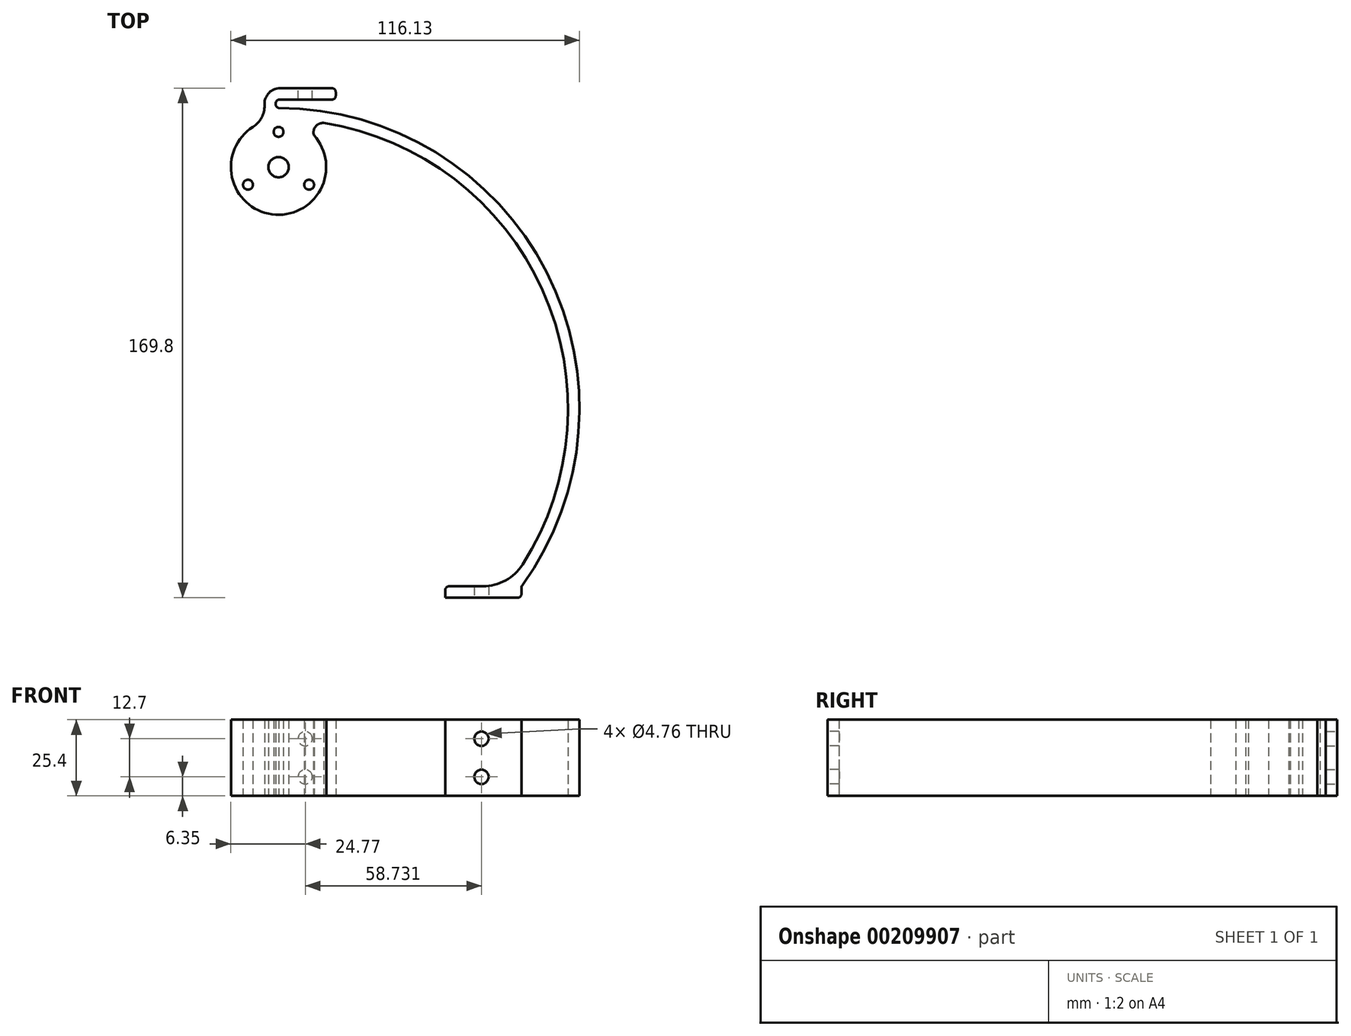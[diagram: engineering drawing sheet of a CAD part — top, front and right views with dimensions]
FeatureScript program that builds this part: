
annotation { "Feature Type Name" : "Feature", "Feature Type Description" : "" }
export const myFeature = defineFeature(function(context is Context, id is Id, definition is map)
    precondition{}
    {
        {
            var Q0;
            Q0=qCreatedBy(makeId("Top.planeOp"),FACE);
            var sketch = newSketch(context, id + "F0", { "sketchPlane" : qUnion([Q0])});
            skCircle(sketch, "E0", {"center": v(0, 0) * mm, "radius": 15.88 * mm});
            skCircle(sketch, "E1", {"center": v(0, 0) * mm, "radius": 3.38 * mm});
            skArc(sketch, "E2", {"start": v(76.2, -139.7) * mm, "mid": v(0, 15.88) * mm, "end": v(-76.2, -139.7) * mm});
            skLineSegment(sketch, "E3", {"start": v(-76.2, -139.7) * mm, "end": v(76.2, -139.7) * mm, "construction": true});
            skLineSegment(sketch, "E4", {"start": v(0, 15.88) * mm, "end": v(0, -139.7) * mm, "construction": true});
            skArc(sketch, "E5.0", {"start": v(81.2, -139.37) * mm, "mid": v(-0.2, 19.67) * mm, "end": v(-80.96, -139.7) * mm});
            skLineSegment(sketch, "E6", {"start": v(56.83, -139.7) * mm, "end": v(80.96, -139.7) * mm, "construction": true});
            skLineSegment(sketch, "E7", {"start": v(76.2, -139.7) * mm, "end": v(55.56, -139.7) * mm});
            skLineSegment(sketch, "E8", {"start": v(55.56, -140.97) * mm, "end": v(55.56, -143.5) * mm});
            skLineSegment(sketch, "E9", {"start": v(55.56, -143.5) * mm, "end": v(79.69, -143.5) * mm});
            skLineSegment(sketch, "E10", {"start": v(80.96, -142.23) * mm, "end": v(80.96, -140.11) * mm});
            skLineSegment(sketch, "E11", {"start": v(0, 19.67) * mm, "end": v(0, 15.88) * mm});
            skLineSegment(sketch, "E12.bottom", {"start": v(0, 26.3) * mm, "end": v(17.78, 26.3) * mm});
            skLineSegment(sketch, "E12.top", {"start": v(0, 22.5) * mm, "end": v(17.78, 22.5) * mm});
            skLineSegment(sketch, "E12.left", {"start": v(0, 26.3) * mm, "end": v(0, 22.5) * mm});
            skLineSegment(sketch, "E12.right", {"start": v(19.05, 25.03) * mm, "end": v(19.05, 23.77) * mm});
            skArc(sketch, "E13", {"start": v(0, 22.5) * mm, "mid": v(-1, 21.09) * mm, "end": v(0, 19.68) * mm});
            skArc(sketch, "E14", {"start": v(0, 26.3) * mm, "mid": v(-4.68, 21.09) * mm, "end": v(0, 15.88) * mm});
            skPoint(sketch, "E15.visualSharp", {"position": v(19.05, 26.3) * mm});
            skArc(sketch, "E15.filletArc", {"start": v(19.05, 25.03) * mm, "mid": v(18.68, 25.93) * mm, "end": v(17.78, 26.3) * mm});
            skPoint(sketch, "E16.visualSharp", {"position": v(19.05, 22.5) * mm});
            skArc(sketch, "E16.filletArc", {"start": v(17.78, 22.5) * mm, "mid": v(18.68, 22.87) * mm, "end": v(19.05, 23.77) * mm});
            skPoint(sketch, "E17.visualSharp", {"position": v(80.96, -143.5) * mm});
            skArc(sketch, "E17.filletArc", {"start": v(79.69, -143.5) * mm, "mid": v(80.58, -143.13) * mm, "end": v(80.96, -142.23) * mm});
            skPoint(sketch, "E18.visualSharp", {"position": v(80.96, -139.7) * mm});
            skArc(sketch, "E18.filletArc", {"start": v(81.2, -139.37) * mm, "mid": v(81.02, -139.72) * mm, "end": v(80.96, -140.11) * mm});
            skPoint(sketch, "E19.newPointB", {"position": v(55.56, -139.7) * mm});
            skArc(sketch, "E19.filletArc", {"start": v(56.83, -139.7) * mm, "mid": v(55.93, -140.07) * mm, "end": v(55.56, -140.97) * mm});
            skLineSegment(sketch, "E20", {"start": v(55.56, -139.7) * mm, "end": v(55.56, -140.97) * mm, "construction": true});
            skLineSegment(sketch, "E21", {"start": v(79.69, -143.5) * mm, "end": v(80.96, -143.5) * mm, "construction": true});
            skLineSegment(sketch, "E22", {"start": v(80.96, -142.23) * mm, "end": v(80.96, -143.5) * mm, "construction": true});
            skArc(sketch, "E23", {"start": v(-8.52, 13.4) * mm, "mid": v(-5.53, 16.7) * mm, "end": v(-4.68, 21.09) * mm});
            skArc(sketch, "E24", {"start": v(15.43, 14.63) * mm, "mid": v(11.9, 12.78) * mm, "end": v(13.1, 8.97) * mm});
            skCircle(sketch, "E25", {"center": v(0, 0) * mm, "radius": 11.75 * mm, "construction": true});
            skCircle(sketch, "E26", {"center": v(0, 11.75) * mm, "radius": 1.65 * mm});
            skCircle(sketch, "E27", {"center": v(10.17, -5.87) * mm, "radius": 1.65 * mm});
            skCircle(sketch, "E28", {"center": v(-10.17, -5.87) * mm, "radius": 1.65 * mm});
            skLineSegment(sketch, "E29", {"start": v(0, 11.75) * mm, "end": v(-10.17, -5.87) * mm, "construction": true});
            skLineSegment(sketch, "E30", {"start": v(10.17, -5.87) * mm, "end": v(0, 11.75) * mm, "construction": true});
            skLineSegment(sketch, "E31", {"start": v(10.17, -5.87) * mm, "end": v(-10.17, -5.87) * mm, "construction": true});
            skLineSegment(sketch, "E32", {"start": v(-10.17, -5.87) * mm, "end": v(5.09, 2.94) * mm, "construction": true});
            skSolve(sketch);
        }
        {
            var Q0;
            Q0 = qSketchRegion(id + "F0", true);
            extrude(context, id + "F1", {"entities" : qUnion([Q0]), "depth" : 25.4 * mm});
        }
        {
            var Q0;
            Q0=makeQuery(id+"F1.opExtrude","SWEPT_EDGE",EDGE,{"disambiguationData":[OSD([sQuery(id+"F0.wireOp",EDGE,"E2"),sQuery(id+"F0.wireOp",EDGE,"E7")])]});
            fillet(context, id + "F2", {"entities" : qUnion([Q0]), "radius" : 15.66 * mm, "tangentPropagation" : true, "allowEdgeOverflow" : false});
        }
        {
            var Q0;
            Q0=makeQuery(id+"F1.opExtrude","SWEPT_FACE",FACE,{"disambiguationData":[OSD([sQuery(id+"F0.wireOp",EDGE,"E9")])]});
            var sketch = newSketch(context, id + "F3", { "sketchPlane" : qUnion([Q0])});
            skLineSegment(sketch, "E33", {"start": v(67.62, 25.4) * mm, "end": v(67.62, 0) * mm, "construction": true});
            skPoint(sketch, "E34", {"position": v(67.62, 19.05) * mm});
            skPoint(sketch, "E35", {"position": v(67.62, 6.35) * mm});
            skSolve(sketch);
        }
        {
            var Q0;
            Q0=sQuery(id+"F3.wireOp",VERTEX,"E34");
            var Q1;
            Q1=sQuery(id+"F3.wireOp",VERTEX,"E35");
            var Q2;
            Q2=makeQuery(id+"F1.opExtrude","SWEPT_BODY",BODY,{"disambiguationData":[OSD([sQuery(id+"F0.wireOp",EDGE,"E0"),sQuery(id+"F0.wireOp",EDGE,"E1"),sQuery(id+"F0.wireOp",EDGE,"E2"),sQuery(id+"F0.wireOp",EDGE,"E5.0"),sQuery(id+"F0.wireOp",EDGE,"E7"),sQuery(id+"F0.wireOp",EDGE,"E8"),sQuery(id+"F0.wireOp",EDGE,"E9"),sQuery(id+"F0.wireOp",EDGE,"E10"),sQuery(id+"F0.wireOp",EDGE,"E12.bottom"),sQuery(id+"F0.wireOp",EDGE,"E12.top"),sQuery(id+"F0.wireOp",EDGE,"E12.right"),sQuery(id+"F0.wireOp",EDGE,"E13"),sQuery(id+"F0.wireOp",EDGE,"E14"),sQuery(id+"F0.wireOp",EDGE,"E15.filletArc"),sQuery(id+"F0.wireOp",EDGE,"E16.filletArc"),sQuery(id+"F0.wireOp",EDGE,"E17.filletArc"),sQuery(id+"F0.wireOp",EDGE,"E18.filletArc"),sQuery(id+"F0.wireOp",EDGE,"E19.filletArc"),sQuery(id+"F0.wireOp",EDGE,"E23"),sQuery(id+"F0.wireOp",EDGE,"E24")])]});
            hole(context, id + "F4", {"style" : HoleStyle.SIMPLE, "endStyle" : HoleEndStyle.BLIND, "holeDiameter" : 4.76 * mm, "holeDepth" : 12.7 * mm, "locations" : qUnion([Q0, Q1]), "scope" : qUnion([Q2])});
        }
        {
            var Q0;
            Q0=makeQuery(id+"F1.opExtrude","SWEPT_FACE",FACE,{"disambiguationData":[OSD([sQuery(id+"F0.wireOp",EDGE,"E12.bottom")])]});
            var sketch = newSketch(context, id + "F5", { "sketchPlane" : qUnion([Q0])});
            skLineSegment(sketch, "E36", {"start": v(-8.9, 0) * mm, "end": v(-8.9, 25.4) * mm, "construction": true});
            skPoint(sketch, "E37", {"position": v(-8.9, 6.35) * mm});
            skPoint(sketch, "E38", {"position": v(-8.9, 19.05) * mm});
            skSolve(sketch);
        }
        {
            var Q0;
            Q0=sQuery(id+"F5.wireOp",VERTEX,"E37");
            var Q1;
            Q1=sQuery(id+"F5.wireOp",VERTEX,"E38");
            var Q2;
            Q2=makeQuery(id+"F1.opExtrude","SWEPT_BODY",BODY,{"disambiguationData":[OSD([sQuery(id+"F0.wireOp",EDGE,"E0"),sQuery(id+"F0.wireOp",EDGE,"E1"),sQuery(id+"F0.wireOp",EDGE,"E2"),sQuery(id+"F0.wireOp",EDGE,"E5.0"),sQuery(id+"F0.wireOp",EDGE,"E7"),sQuery(id+"F0.wireOp",EDGE,"E8"),sQuery(id+"F0.wireOp",EDGE,"E9"),sQuery(id+"F0.wireOp",EDGE,"E10"),sQuery(id+"F0.wireOp",EDGE,"E12.bottom"),sQuery(id+"F0.wireOp",EDGE,"E12.top"),sQuery(id+"F0.wireOp",EDGE,"E12.right"),sQuery(id+"F0.wireOp",EDGE,"E13"),sQuery(id+"F0.wireOp",EDGE,"E14"),sQuery(id+"F0.wireOp",EDGE,"E15.filletArc"),sQuery(id+"F0.wireOp",EDGE,"E16.filletArc"),sQuery(id+"F0.wireOp",EDGE,"E17.filletArc"),sQuery(id+"F0.wireOp",EDGE,"E18.filletArc"),sQuery(id+"F0.wireOp",EDGE,"E19.filletArc"),sQuery(id+"F0.wireOp",EDGE,"E23"),sQuery(id+"F0.wireOp",EDGE,"E24")])]});
            hole(context, id + "F6", {"style" : HoleStyle.SIMPLE, "endStyle" : HoleEndStyle.BLIND, "holeDiameter" : 4.76 * mm, "holeDepth" : 5.08 * mm, "startFromSketch" : true, "locations" : qUnion([Q0, Q1]), "scope" : qUnion([Q2])});
        }
    });
